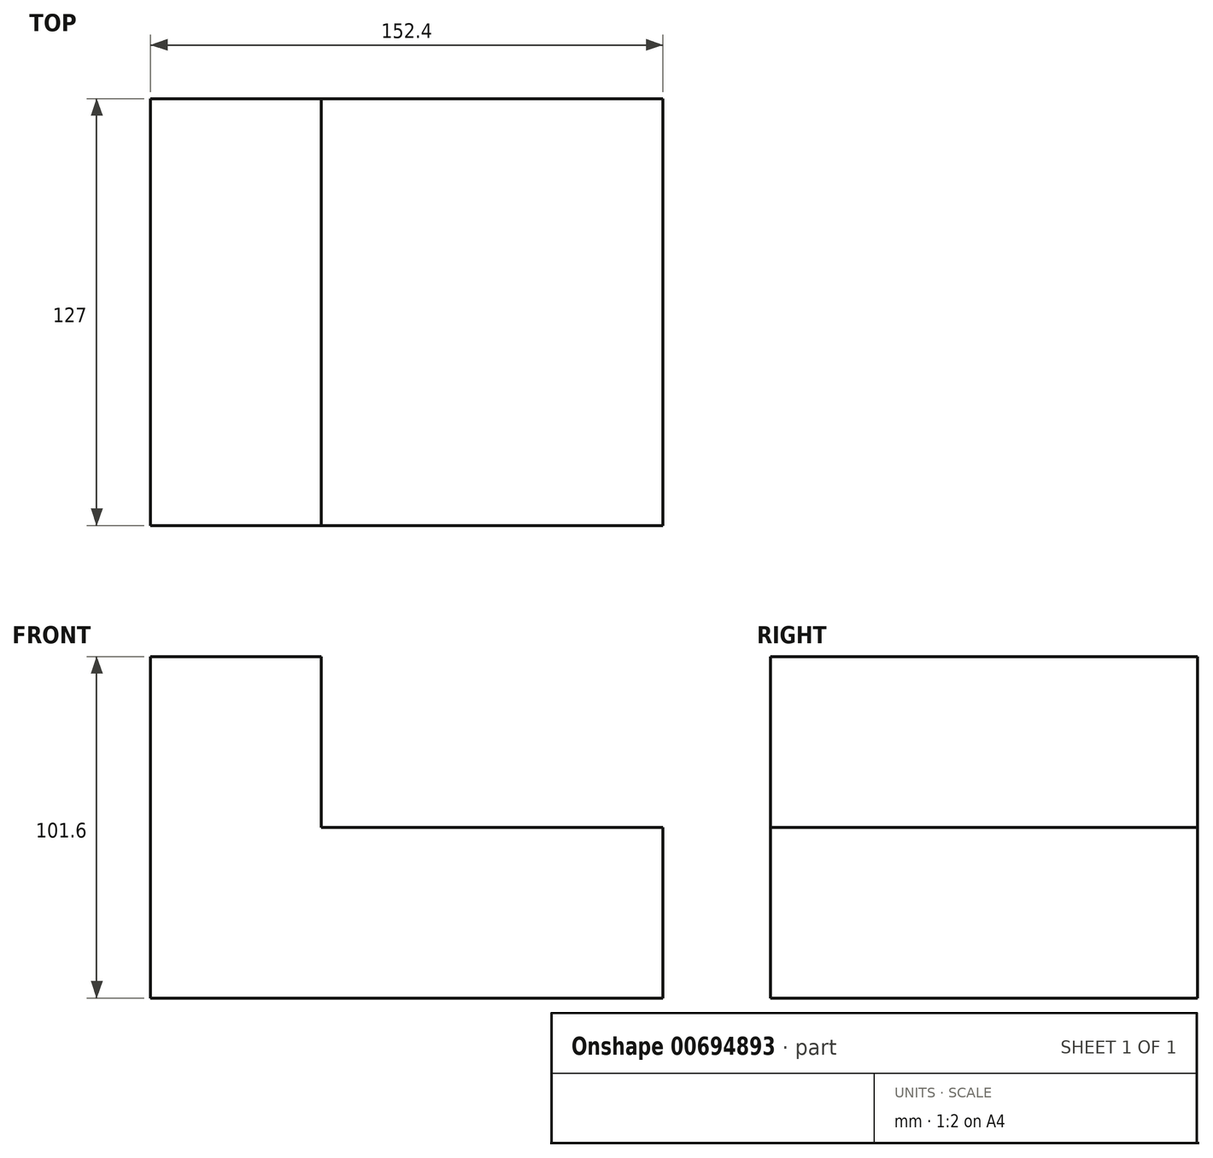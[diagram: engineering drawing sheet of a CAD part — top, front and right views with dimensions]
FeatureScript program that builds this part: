
annotation { "Feature Type Name" : "Feature", "Feature Type Description" : "" }
export const myFeature = defineFeature(function(context is Context, id is Id, definition is map)
    precondition{}
    {
        {
            var Q0;
            Q0=qCreatedBy(makeId("Front.planeOp"),FACE);
            var sketch = newSketch(context, id + "F0", { "sketchPlane" : qUnion([Q0])});
            skLineSegment(sketch, "E0.bottom", {"start": v(0, 0) * mm, "end": v(50.8, 0) * mm});
            skLineSegment(sketch, "E0.top", {"start": v(0, 101.6) * mm, "end": v(50.8, 101.6) * mm});
            skLineSegment(sketch, "E0.left", {"start": v(0, 0) * mm, "end": v(0, 101.6) * mm});
            skLineSegment(sketch, "E0.right", {"start": v(50.8, 0) * mm, "end": v(50.8, 101.6) * mm});
            skLineSegment(sketch, "E1.bottom", {"start": v(50.8, 0) * mm, "end": v(152.4, 0) * mm});
            skLineSegment(sketch, "E1.top", {"start": v(50.8, 50.8) * mm, "end": v(152.4, 50.8) * mm});
            skLineSegment(sketch, "E1.left", {"start": v(50.8, 0) * mm, "end": v(50.8, 50.8) * mm});
            skLineSegment(sketch, "E1.right", {"start": v(152.4, 0) * mm, "end": v(152.4, 50.8) * mm});
            skSolve(sketch);
        }
        {
            var Q0;
            Q0=makeQuery(id+"F0.imprint","IMPRINT",FACE,{"disambiguationData":[TD([[makeQuery(id+"F0.imprint","IMPRINT",EDGE,{"derivedFrom":sQuery(id+"F0.wireOp",EDGE,"E0.bottom")}),1.0]])]});
            var Q1;
            Q1=makeQuery(id+"F0.imprint","IMPRINT",FACE,{"disambiguationData":[TD([[makeQuery(id+"F0.imprint","IMPRINT",EDGE,{"derivedFrom":sQuery(id+"F0.wireOp",EDGE,"E1.bottom")}),1.0]])]});
            extrude(context, id + "F1", {"entities" : qUnion([Q0, Q1]), "depth" : 127 * mm, "offsetDistance" : 25.4 * mm});
        }
    });
